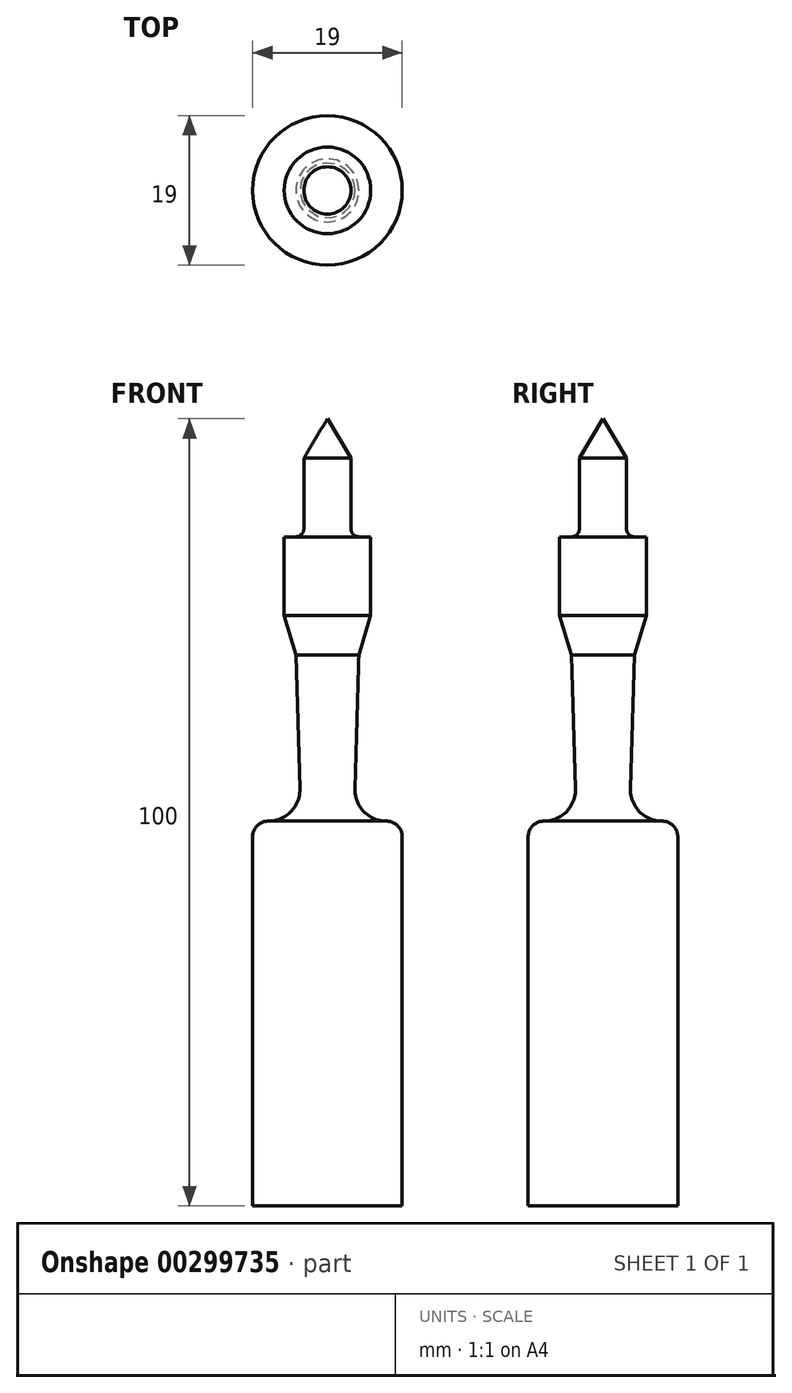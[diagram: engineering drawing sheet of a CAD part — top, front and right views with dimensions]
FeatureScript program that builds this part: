
annotation { "Feature Type Name" : "Feature", "Feature Type Description" : "" }
export const myFeature = defineFeature(function(context is Context, id is Id, definition is map)
    precondition{}
    {
        {
            var Q0;
            Q0=qCreatedBy(makeId("Front.planeOp"),FACE);
            var sketch = newSketch(context, id + "F0", { "sketchPlane" : qUnion([Q0])});
            skLineSegment(sketch, "E0", {"start": v(0, 0) * mm, "end": v(0, -100) * mm});
            skLineSegment(sketch, "E1", {"start": v(0, 0) * mm, "end": v(3, -5) * mm});
            skLineSegment(sketch, "E2", {"start": v(3, -5) * mm, "end": v(3, -14) * mm});
            skArc(sketch, "E3", {"start": v(3, -14) * mm, "mid": v(3.3, -14.7) * mm, "end": v(4, -15) * mm});
            skLineSegment(sketch, "E4", {"start": v(4, -15) * mm, "end": v(5.5, -15) * mm});
            skLineSegment(sketch, "E5", {"start": v(5.5, -15) * mm, "end": v(5.5, -25) * mm});
            skLineSegment(sketch, "E6", {"start": v(5.5, -25) * mm, "end": v(4, -30) * mm});
            skLineSegment(sketch, "E7", {"start": v(4, -30) * mm, "end": v(3.5, -47) * mm});
            skLineSegment(sketch, "E8", {"start": v(9.5, -53.12) * mm, "end": v(9.5, -100) * mm});
            skLineSegment(sketch, "E9", {"start": v(9.5, -100) * mm, "end": v(0, -100) * mm});
            skArc(sketch, "E10", {"start": v(3.5, -47) * mm, "mid": v(4.63, -49.9) * mm, "end": v(7.5, -51.12) * mm});
            skArc(sketch, "E11", {"start": v(9.5, -53.12) * mm, "mid": v(8.91, -51.7) * mm, "end": v(7.5, -51.12) * mm});
            skSolve(sketch);
        }
        {
            var Q0;
            Q0=makeQuery(id+"F0.imprint","IMPRINT",FACE,{"disambiguationData":[TD([[makeQuery(id+"F0.imprint","IMPRINT",EDGE,{"derivedFrom":sQuery(id+"F0.wireOp",EDGE,"E0")}),1.0]])]});
            var Q1;
            Q1=sQuery(id+"F0.wireOp",EDGE,"E0");
            revolve(context, id + "F1", {"entities" : qUnion([Q0]), "axis" : qUnion([Q1]), "revolveType" : RevolveType.FULL});
        }
    });
